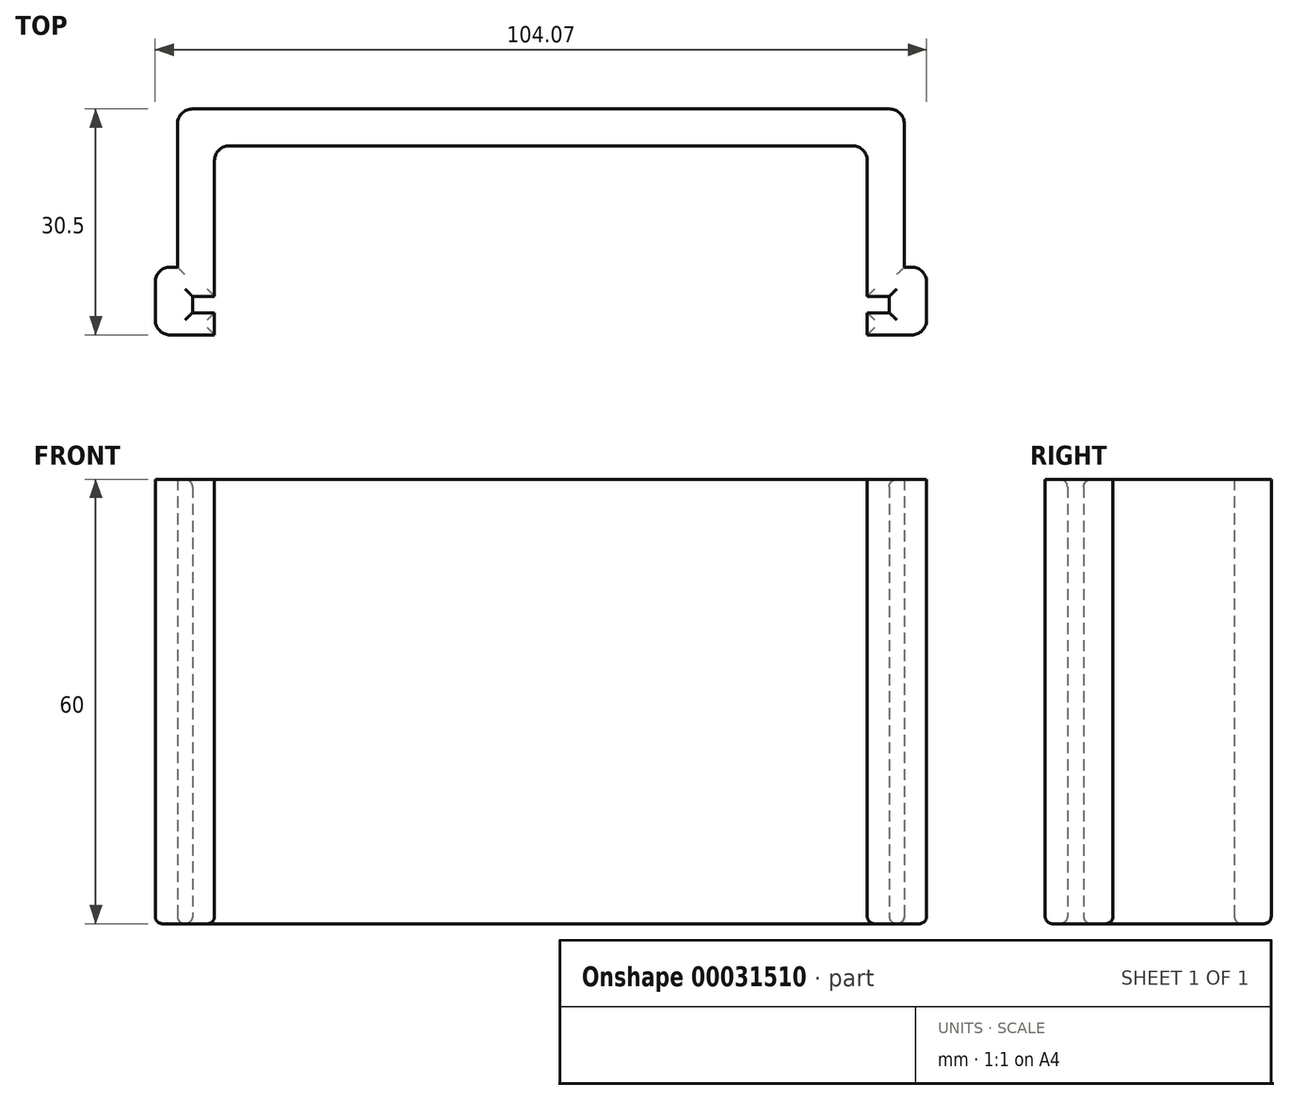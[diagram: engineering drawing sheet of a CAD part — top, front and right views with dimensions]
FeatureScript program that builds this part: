
annotation { "Feature Type Name" : "Feature", "Feature Type Description" : "" }
export const myFeature = defineFeature(function(context is Context, id is Id, definition is map)
    precondition{}
    {
        {
            var Q0;
            Q0=qCreatedBy(makeId("Top.planeOp"),FACE);
            var sketch = newSketch(context, id + "F0", { "sketchPlane" : qUnion([Q0])});
            skLineSegment(sketch, "E0.bottom", {"start": v(-22, 12.95) * mm, "end": v(76.06, 12.95) * mm});
            skLineSegment(sketch, "E0.top", {"start": v(-22, -17.55) * mm, "end": v(76.06, -17.55) * mm});
            skLineSegment(sketch, "E0.left", {"start": v(-22, 12.95) * mm, "end": v(-22, -17.55) * mm});
            skLineSegment(sketch, "E0.right", {"start": v(76.06, 12.95) * mm, "end": v(76.06, -17.55) * mm});
            skLineSegment(sketch, "E1.bottom", {"start": v(-17, 7.98) * mm, "end": v(71.06, 7.98) * mm});
            skLineSegment(sketch, "E1.top", {"start": v(-17, -17.55) * mm, "end": v(71.06, -17.55) * mm});
            skLineSegment(sketch, "E1.left", {"start": v(-17, 7.98) * mm, "end": v(-17, -17.55) * mm});
            skLineSegment(sketch, "E1.right", {"start": v(71.06, 7.98) * mm, "end": v(71.06, -17.55) * mm});
            skLineSegment(sketch, "E2.bottom", {"start": v(-17, -14.55) * mm, "end": v(-19.97, -14.55) * mm});
            skLineSegment(sketch, "E2.top", {"start": v(-17, -12.35) * mm, "end": v(-19.97, -12.35) * mm});
            skLineSegment(sketch, "E2.left", {"start": v(-17, -14.55) * mm, "end": v(-17, -12.35) * mm});
            skLineSegment(sketch, "E2.right", {"start": v(-19.97, -14.55) * mm, "end": v(-19.97, -12.35) * mm});
            skLineSegment(sketch, "E3.bottom", {"start": v(71.06, -12.35) * mm, "end": v(74.03, -12.35) * mm});
            skLineSegment(sketch, "E3.top", {"start": v(71.06, -14.55) * mm, "end": v(74.03, -14.55) * mm});
            skLineSegment(sketch, "E3.left", {"start": v(71.06, -12.35) * mm, "end": v(71.06, -14.55) * mm});
            skLineSegment(sketch, "E3.right", {"start": v(74.03, -12.35) * mm, "end": v(74.03, -14.55) * mm});
            skLineSegment(sketch, "E4.bottom", {"start": v(-25, -8.4) * mm, "end": v(-22, -8.4) * mm});
            skLineSegment(sketch, "E4.top", {"start": v(-25, -17.55) * mm, "end": v(-22, -17.55) * mm});
            skLineSegment(sketch, "E4.left", {"start": v(-25, -8.4) * mm, "end": v(-25, -17.55) * mm});
            skLineSegment(sketch, "E4.right", {"start": v(-22, -8.4) * mm, "end": v(-22, -17.55) * mm});
            skLineSegment(sketch, "E5.bottom", {"start": v(76.06, -8.4) * mm, "end": v(79.06, -8.4) * mm});
            skLineSegment(sketch, "E5.top", {"start": v(76.06, -17.55) * mm, "end": v(79.06, -17.55) * mm});
            skLineSegment(sketch, "E5.left", {"start": v(76.06, -8.4) * mm, "end": v(76.06, -17.55) * mm});
            skLineSegment(sketch, "E5.right", {"start": v(79.06, -8.4) * mm, "end": v(79.06, -17.55) * mm});
            skSolve(sketch);
        }
        {
            var Q0;
            Q0=makeQuery(id+"F0.imprint","IMPRINT",FACE,{"disambiguationData":[TD([[makeQuery(id+"F0.imprint","IMPRINT",EDGE,{"derivedFrom":sQuery(id+"F0.wireOp",EDGE,"E4.bottom")}),-1.0]])]});
            var Q1;
            Q1=makeQuery(id+"F0.imprint","IMPRINT",FACE,{"disambiguationData":[TD([[makeQuery(id+"F0.imprint","IMPRINT",EDGE,{"derivedFrom":sQuery(id+"F0.wireOp",EDGE,"E0.bottom")}),-1.0]])]});
            var Q2;
            Q2=makeQuery(id+"F0.imprint","IMPRINT",FACE,{"disambiguationData":[TD([[makeQuery(id+"F0.imprint","IMPRINT",EDGE,{"derivedFrom":sQuery(id+"F0.wireOp",EDGE,"E5.bottom")}),-1.0]])]});
            extrude(context, id + "F1", {"entities" : qUnion([Q0, Q1, Q2]), "depth" : 60 * mm});
        }
        {
            var Q0;
            Q0=makeQuery(id+"F1.opExtrude","SWEPT_EDGE",EDGE,{"disambiguationData":[OSD([sQuery(id+"F0.wireOp",EDGE,"E0.bottom"),sQuery(id+"F0.wireOp",EDGE,"E0.left")])]});
            var Q1;
            Q1=makeQuery(id+"F1.opExtrude","SWEPT_EDGE",EDGE,{"disambiguationData":[OSD([sQuery(id+"F0.wireOp",EDGE,"E0.bottom"),sQuery(id+"F0.wireOp",EDGE,"E0.right")])]});
            var Q2;
            Q2=makeQuery(id+"F1.opExtrude","SWEPT_EDGE",EDGE,{"disambiguationData":[OSD([sQuery(id+"F0.wireOp",EDGE,"E4.bottom"),sQuery(id+"F0.wireOp",EDGE,"E4.left")])]});
            var Q3;
            Q3=makeQuery(id+"F1.opExtrude","SWEPT_EDGE",EDGE,{"disambiguationData":[OSD([sQuery(id+"F0.wireOp",EDGE,"E4.top"),sQuery(id+"F0.wireOp",EDGE,"E4.left")])]});
            var Q4;
            Q4=makeQuery(id+"F1.opExtrude","SWEPT_EDGE",EDGE,{"disambiguationData":[OSD([sQuery(id+"F0.wireOp",EDGE,"E5.bottom"),sQuery(id+"F0.wireOp",EDGE,"E5.right")])]});
            var Q5;
            Q5=makeQuery(id+"F1.opExtrude","SWEPT_EDGE",EDGE,{"disambiguationData":[OSD([sQuery(id+"F0.wireOp",EDGE,"E5.top"),sQuery(id+"F0.wireOp",EDGE,"E5.right")])]});
            var Q6;
            Q6=makeQuery(id+"F1.opExtrude","SWEPT_EDGE",EDGE,{"disambiguationData":[OSD([sQuery(id+"F0.wireOp",EDGE,"E1.bottom"),sQuery(id+"F0.wireOp",EDGE,"E1.left")])]});
            var Q7;
            Q7=makeQuery(id+"F1.opExtrude","SWEPT_EDGE",EDGE,{"disambiguationData":[OSD([sQuery(id+"F0.wireOp",EDGE,"E1.bottom"),sQuery(id+"F0.wireOp",EDGE,"E1.right")])]});
            fillet(context, id + "F2", {"entities" : qUnion([Q0, Q1, Q2, Q3, Q4, Q5, Q6, Q7]), "radius" : 2 * mm, "tangentPropagation" : true, "allowEdgeOverflow" : false});
        }
        {
            var Q0;
            Q0=makeQuery(id+"F1.opExtrude","CAP_EDGE",EDGE,{"disambiguationData":[OSD([sQuery(id+"F0.wireOp",EDGE,"E2.bottom")])],"isStart":true});
            var Q1;
            Q1=makeQuery(id+"F1.opExtrude","CAP_EDGE",EDGE,{"disambiguationData":[OSD([sQuery(id+"F0.wireOp",EDGE,"E2.top")])],"isStart":true});
            var Q2;
            Q2=makeQuery(id+"F1.opExtrude","CAP_EDGE",EDGE,{"disambiguationData":[OSD([sQuery(id+"F0.wireOp",EDGE,"E2.right")])],"isStart":true});
            var Q3;
            Q3=makeQuery(id+"F1.opExtrude","CAP_EDGE",EDGE,{"disambiguationData":[OSD([sQuery(id+"F0.wireOp",EDGE,"E2.top")])],"isStart":false});
            var Q4;
            Q4=makeQuery(id+"F1.opExtrude","CAP_EDGE",EDGE,{"disambiguationData":[OSD([sQuery(id+"F0.wireOp",EDGE,"E2.right")])],"isStart":false});
            var Q5;
            Q5=makeQuery(id+"F1.opExtrude","CAP_EDGE",EDGE,{"disambiguationData":[OSD([sQuery(id+"F0.wireOp",EDGE,"E2.bottom")])],"isStart":false});
            var Q6;
            Q6=makeQuery(id+"F1.opExtrude","CAP_EDGE",EDGE,{"disambiguationData":[OSD([sQuery(id+"F0.wireOp",EDGE,"E3.top")])],"isStart":true});
            var Q7;
            Q7=makeQuery(id+"F1.opExtrude","CAP_FACE",FACE,{"disambiguationData":[OSD([sQuery(id+"F0.wireOp",EDGE,"E0.bottom"),sQuery(id+"F0.wireOp",EDGE,"E0.top"),sQuery(id+"F0.wireOp",EDGE,"E0.left"),sQuery(id+"F0.wireOp",EDGE,"E0.right"),sQuery(id+"F0.wireOp",EDGE,"E1.bottom"),sQuery(id+"F0.wireOp",EDGE,"E1.left"),sQuery(id+"F0.wireOp",EDGE,"E1.right"),sQuery(id+"F0.wireOp",EDGE,"E2.bottom"),sQuery(id+"F0.wireOp",EDGE,"E2.top"),sQuery(id+"F0.wireOp",EDGE,"E2.right"),sQuery(id+"F0.wireOp",EDGE,"E3.bottom"),sQuery(id+"F0.wireOp",EDGE,"E3.top"),sQuery(id+"F0.wireOp",EDGE,"E3.right"),sQuery(id+"F0.wireOp",EDGE,"E4.bottom"),sQuery(id+"F0.wireOp",EDGE,"E4.top"),sQuery(id+"F0.wireOp",EDGE,"E4.left"),sQuery(id+"F0.wireOp",EDGE,"E5.bottom"),sQuery(id+"F0.wireOp",EDGE,"E5.top"),sQuery(id+"F0.wireOp",EDGE,"E5.right")])],"isStart":true});
            var Q8;
            Q8=makeQuery(id+"F1.opExtrude","CAP_EDGE",EDGE,{"disambiguationData":[OSD([sQuery(id+"F0.wireOp",EDGE,"E3.right")])],"isStart":true});
            var Q9;
            Q9=makeQuery(id+"F1.opExtrude","CAP_EDGE",EDGE,{"disambiguationData":[OSD([sQuery(id+"F0.wireOp",EDGE,"E3.top")])],"isStart":false});
            var Q10;
            Q10=makeQuery(id+"F1.opExtrude","CAP_EDGE",EDGE,{"disambiguationData":[OSD([sQuery(id+"F0.wireOp",EDGE,"E3.right")])],"isStart":false});
            var Q11;
            Q11=makeQuery(id+"F1.opExtrude","CAP_EDGE",EDGE,{"disambiguationData":[OSD([sQuery(id+"F0.wireOp",EDGE,"E3.bottom")])],"isStart":false});
            fillet(context, id + "F3", {"entities" : qUnion([Q0, Q1, Q2, Q3, Q4, Q5, Q6, Q7, Q8, Q9, Q10, Q11]), "radius" : 1 * mm, "tangentPropagation" : true, "allowEdgeOverflow" : false});
        }
    });
